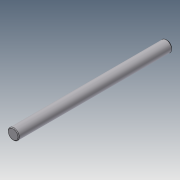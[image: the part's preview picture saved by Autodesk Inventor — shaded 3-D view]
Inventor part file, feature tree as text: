
AUTODESK INVENTOR PART (.ipt)
format: ipt  version: 2018.3 (Build 223284000, 284)  size: 107,520 bytes
history: native  units: in
note: dims shown in document units (in); Inventor stores cm internally (conversion verified against a paired STEP export)
features: hole x2, sketch x2, extrude x1, chamfer x1
ambient origin geometry x8: Origin, YZ Plane, XZ Plane, XY Plane, X Axis, Y Axis, Z Axis, Center Point
bodies: Solid1 (feature_tree)
feature tree (6):
  extrude  "Extrusion1"  Depth=3.52in TaperAngle=0.0deg
  hole  "Hole2"  [1 undecoded]
  chamfer  "Chamfer3"  [1 undecoded]
  hole  "Hole3"  [1 undecoded]
  sketch  "Sketch1"  dims[d0=0.25in d1=3.52in d2=0.0in]
  sketch  "Sketch11"  dims[d32=0.015in d33=0.015in d34=45.0deg d63=1.0in d64=1.0in d56=0.158in d57=0.75in d58=0.178in d59=0.25in d60=90.0deg d61=1.15in d62=0.8108in d65=0.06in d66=0.06in d67=0.75in d68=0.375in d69=0.25in d70=0.5635in d71=0.15in d72=0.8108in]
note: 3 required parameter values undecoded (feature->parameter linkage not recoverable at this tier; creation-order binding heuristic only, values carry confidence <= 0.55)
